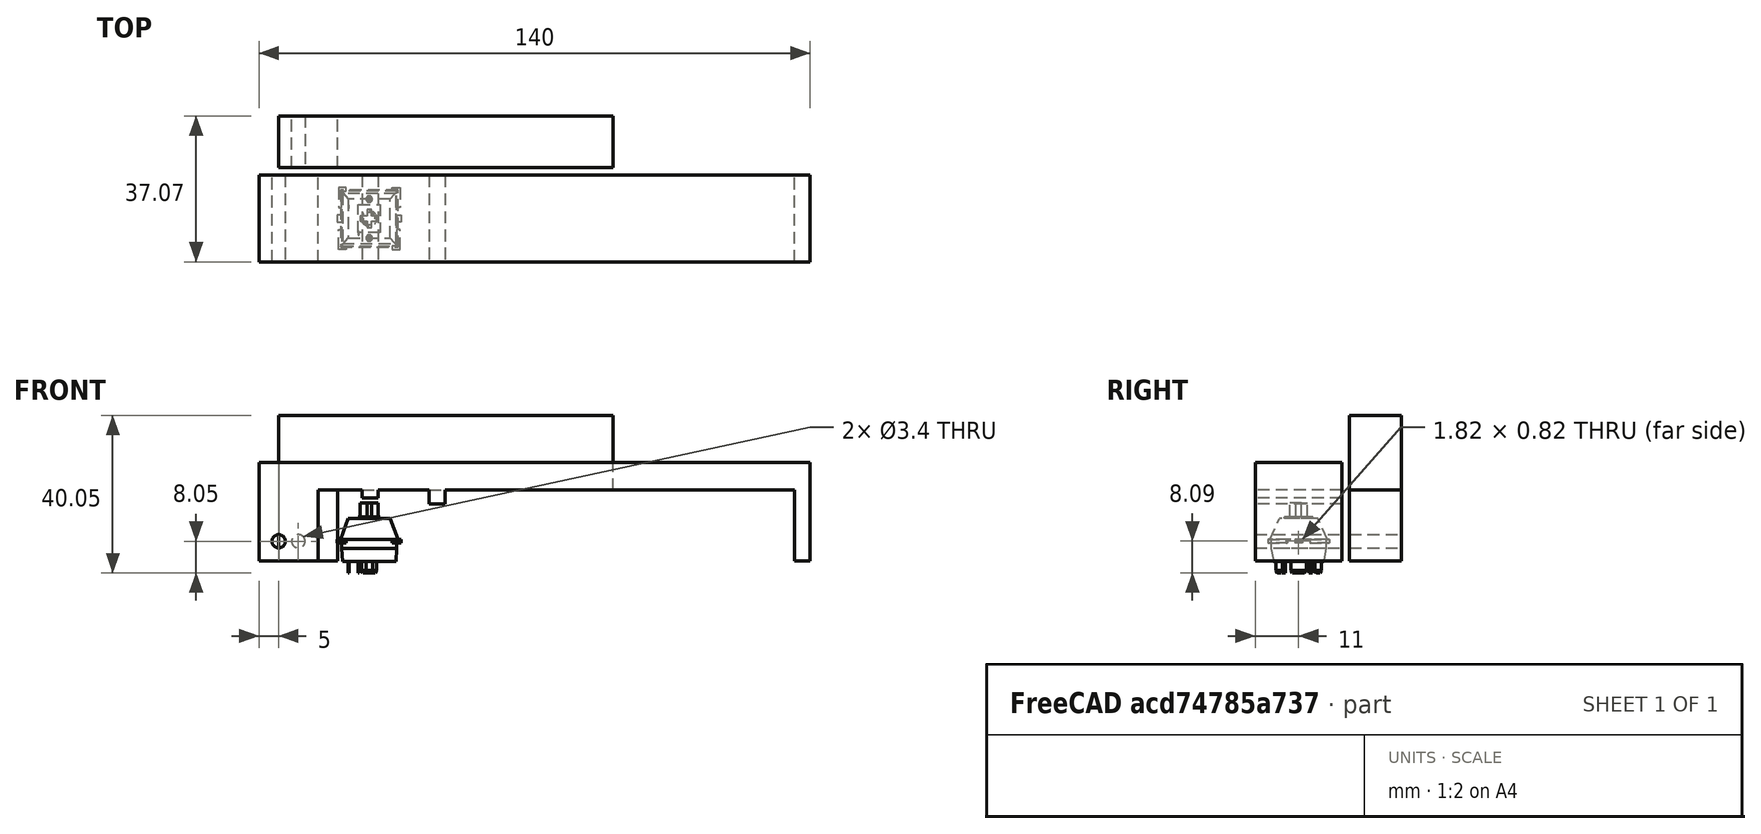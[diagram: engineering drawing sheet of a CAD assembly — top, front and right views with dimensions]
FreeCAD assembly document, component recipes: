
FREECAD ASSEMBLY — COMPONENT RECIPES ("ProtoKeyboardPiano")

This assembly document has 2 components, labeled P0..P1 below (a component is one placed body or linked part). 2 of them carry a construction recipe — the FreeCAD feature program that regenerates the part from scratch, quoted from this document or its linked companion documents; the rest are supplied as boundary geometry only. No exploded tour is included for this assembly.
COMPONENT P0 — recipe-attached ("Part001", modeled in this document).
Construction recipe (the document's own serialized feature program — sketch geometry with constraints, then the solid features built on it; lengths are millimeters unless a unit is written):

FEATURE [Sketcher::SketchObject] Sketch
  ArcFitTolerance = 1e-06
  AttachmentSupport = -> [XZ_Plane]
  FullyConstrained = true
  MakeInternals = false
  MapMode = 5
  Placement = pos=(0,0,0) rot=(1,0,0;1.5708rad)
  sketch-geometry (5):
    g0: Circle CenterX=0 CenterY=0 CenterZ=0 NormalX=0 NormalY=0 NormalZ=1 AngleXU=0 Radius=1.7
    g1: LineSegment StartX=-5 StartY=-5 StartZ=0 EndX=-5 EndY=20 EndZ=0
    g2: LineSegment StartX=-5 StartY=20 StartZ=0 EndX=135 EndY=20 EndZ=0
    g3: LineSegment StartX=135 StartY=20 StartZ=0 EndX=135 EndY=-5 EndZ=0
    g4: LineSegment StartX=135 StartY=-5 StartZ=0 EndX=-5 EndY=-5 EndZ=0
  constraints (14):
    c: Coincident(g0,g-1)
    c: Diameter(g0) = 3.4
    c: Vertical(g1)
    c: Coincident(g1,g2)
    c: Horizontal(g2)
    c: Coincident(g2,g3)
    c: Vertical(g3)
    c: Coincident(g3,g4)
    c: Coincident(g4,g1)
    c: Horizontal(g4)
    c: DistanceX(g2,g2) = 140
    c: DistanceX(g1,g0) = 5
    c: DistanceY(g1,g0) = 5
    c: DistanceY(g3,g3) = 25
FEATURE [PartDesign::Pad] Pad
  Direction = (0,-1,2e-16)
  Length = 22
  Length2 = 10
  Midplane = true
  Placement = pos=(0,0,0) rot=(1,0,0;1.5708rad)
  Profile = -> Sketch
  ReferenceAxis = -> Sketch [N_Axis]
  Refine = true
  Suppressed = false
  Type = 0
FEATURE [Sketcher::SketchObject] Sketch001
  ArcFitTolerance = 1e-06
  AttachmentSupport = -> [XZ_Plane]
  ExternalGeometry = -> [Pad]
  FullyConstrained = true
  MakeInternals = false
  MapMode = 5
  Placement = pos=(0,0,0) rot=(1,0,0;1.5708rad)
  sketch-geometry (4):
    g0: LineSegment StartX=10 StartY=-5 StartZ=0 EndX=131 EndY=-5 EndZ=0
    g1: LineSegment StartX=131 StartY=-5 StartZ=0 EndX=131 EndY=13 EndZ=0
    g2: LineSegment StartX=131 StartY=13 StartZ=0 EndX=10 EndY=13 EndZ=0
    g3: LineSegment StartX=10 StartY=13 StartZ=0 EndX=10 EndY=-5 EndZ=0
  constraints (12):
    c: Coincident(g0,g1)
    c: Coincident(g1,g2)
    c: Coincident(g2,g3)
    c: Coincident(g3,g0)
    c: Horizontal(g0)
    c: Horizontal(g2)
    c: Vertical(g1)
    c: Vertical(g3)
    c: PointOnObject(g0,g-3)
    c: Distance(g-3,g0) = 4
    c: DistanceY(g1,g1) = 18
    c: DistanceX(g-1,g0) = 10
FEATURE [PartDesign::Pocket] Pocket
  BaseFeature = -> Pad
  Direction = (0,1,-2e-16)
  Length = 5
  Length2 = 5
  Midplane = true
  Placement = pos=(0,0,0) rot=(1,0,0;1.5708rad)
  Profile = -> Sketch001
  ReferenceAxis = -> Sketch001 [N_Axis]
  Refine = true
  Suppressed = false
  Type = 1
FEATURE [Sketcher::SketchObject] Sketch002
  ArcFitTolerance = 1e-06
  AttachmentSupport = -> [XZ_Plane]
  ExternalGeometry = -> [Pocket]
  FullyConstrained = false
  MakeInternals = false
  MapMode = 5
  Placement = pos=(0,0,0) rot=(1,0,0;1.5708rad)
  sketch-geometry (23):
    g0: LineSegment [constr] StartX=0 StartY=0 StartZ=0 EndX=0 EndY=13 EndZ=0
    g1: LineSegment [constr] StartX=0 StartY=0 StartZ=0 EndX=1.14262 EndY=12.9497 EndZ=0
    g2: LineSegment [constr] StartX=1.14262 StartY=12.9497 StartZ=0 EndX=131 EndY=1.49168 EndZ=0
    g3: LineSegment [constr] StartX=23.2391 StartY=13 StartZ=0 EndX=23.2391 EndY=11 EndZ=0
    g4: LineSegment [constr] StartX=40.2391 StartY=13 StartZ=0 EndX=40.2391 EndY=9.5 EndZ=0
    g5: LineSegment StartX=21.2391 StartY=11 StartZ=0 EndX=25.2391 EndY=11 EndZ=0
    g6: LineSegment StartX=25.2391 StartY=11 StartZ=0 EndX=25.2391 EndY=13 EndZ=0
    g7: LineSegment StartX=25.2391 StartY=13 StartZ=0 EndX=21.2391 EndY=13 EndZ=0
    g8: LineSegment StartX=21.2391 StartY=13 StartZ=0 EndX=21.2391 EndY=11 EndZ=0
    g9: GeomPoint [constr] X=23.2391 Y=12 Z=0
    g10: LineSegment StartX=38.2391 StartY=9.5 StartZ=0 EndX=42.2391 EndY=9.5 EndZ=0
    g11: LineSegment StartX=42.2391 StartY=9.5 StartZ=0 EndX=42.2391 EndY=13 EndZ=0
    g12: LineSegment StartX=42.2391 StartY=13 StartZ=0 EndX=38.2391 EndY=13 EndZ=0
    g13: LineSegment StartX=38.2391 StartY=13 StartZ=0 EndX=38.2391 EndY=9.5 EndZ=0
    g14: GeomPoint [constr] X=40.2391 Y=11.25 Z=0
    g15: LineSegment [constr] StartX=0 StartY=13 StartZ=0 EndX=131 EndY=13 EndZ=0
    g16: LineSegment [constr] StartX=131 StartY=13 StartZ=0 EndX=131 EndY=1.49168 EndZ=0
    g17: LineSegment [constr] StartX=80 StartY=13 StartZ=0 EndX=80 EndY=-14.9258 EndZ=0
    g18: LineSegment [constr] StartX=0 StartY=0 StartZ=0 EndX=1.94118 EndY=16.5 EndZ=0
    g19: LineSegment [constr] StartX=1.94118 StartY=16.5 StartZ=0 EndX=80 EndY=7.31663 EndZ=0
    g20: LineSegment [constr] StartX=0 StartY=11.9944 StartZ=0 EndX=80 EndY=11.9944 EndZ=0
    g21: LineSegment [constr] StartX=57.2391 StartY=11.9944 StartZ=0 EndX=57.2391 EndY=9.99439 EndZ=0
    g22: LineSegment [constr] StartX=74.2391 StartY=11.9944 StartZ=0 EndX=74.2391 EndY=7.99439 EndZ=0
  constraints (68):
    c: Coincident(g0,g-1)
    c: PointOnObject(g0,g-2)
    c: Coincident(g0,g1)
    c: Coincident(g1,g2)
    c: Perpendicular(g2,g1,g1) = 1.5708
    c: Equal(g0,g1)
    c: PointOnObject(g3,g2)
    c: Vertical(g3)
    c: PointOnObject(g4,g2)
    c: Vertical(g4)
    c: Distance(g3,g3) = 2
    c: Distance(g4,g4) = 3.5
    c: DistanceX(g0,g3) = 23.2391
    c: DistanceX(g0,g4) = 40.2391
    c: Coincident(g5,g6)
    c: Coincident(g6,g7)
    c: Coincident(g7,g8)
    c: Coincident(g8,g5)
    c: Horizontal(g5)
    c: Horizontal(g7)
    c: Vertical(g6)
    c: Vertical(g8)
    c: Symmetric(g7,g5,g9)
    c: Symmetric(g3,g3,g9)
    c: Coincident(g10,g11)
    c: Coincident(g11,g12)
    c: Coincident(g12,g13)
    c: Coincident(g13,g10)
    c: Horizontal(g10)
    c: Horizontal(g12)
    c: Vertical(g11)
    c: Vertical(g13)
    c: Symmetric(g12,g10,g14)
    c: Symmetric(g4,g4,g14)
    c: Equal(g12,g7)
    c: Distance(g7,g7) = 4
    c: Coincident(g15,g0)
    c: Horizontal(g15)
    c: PointOnObject(g6,g15)
    c: PointOnObject(g3,g5)
    c: PointOnObject(g11,g15)
    c: PointOnObject(g4,g10)
    c: Coincident(g16,g15)
    c: Coincident(g16,g2)
    c: Perpendicular(g15,g16)
    c: Vertical(g17)
    c: DistanceX(g17,g-4) = 55
    c: Coincident(g15,g-3)
    c: PointOnObject(g17,g15)
    c: Coincident(g18,g0)
    c: Coincident(g19,g18)
    c: Perpendicular(g19,g18)
    c: PointOnObject(g19,g17)
    c: PointOnObject(g20,g-2)
    c: Horizontal(g20)
    c: PointOnObject(g20,g17)
    c: PointOnObject(g21,g20)
    c: PointOnObject(g21,g19)
    c: Vertical(g21)
    c: PointOnObject(g22,g20)
    c: PointOnObject(g22,g19)
    c: Vertical(g22)
    c: Distance(g21,g21) = 2
    c: Distance(g22,g22) = 4
    c: DistanceX(g3,g4) = 17
    c: DistanceX(g4,g21) = 17
    c: DistanceX(g21,g22) = 17
    c: DistanceY(g16,g16) = 11.5083
FEATURE [PartDesign::Pad] Pad001
  BaseFeature = -> Pocket
  Direction = (0,-1,2e-16)
  Length = 22
  Length2 = 10
  Midplane = true
  Placement = pos=(0,0,0) rot=(1,0,0;1.5708rad)
  Profile = -> Sketch002
  ReferenceAxis = -> Sketch002 [N_Axis]
  Refine = true
  Suppressed = false
  Type = 0
FEATURE [PartDesign::Body] Body  label="Corps"
  AllowCompound = false
  Group = -> [Sketch,Pad,Sketch001,Pocket,Sketch002,Pad001]
  Origin = -> Origin
  Tip = -> Pad001
COMPONENT P1 — recipe-attached ("Part002", modeled in this document).
Construction recipe (the document's own serialized feature program — sketch geometry with constraints, then the solid features built on it; lengths are millimeters unless a unit is written):

FEATURE [Sketcher::SketchObject] Sketch004
  ArcFitTolerance = 1e-06
  AttachmentSupport = -> [XZ_Plane003]
  FullyConstrained = true
  MakeInternals = false
  MapMode = 5
  Placement = pos=(0,0,0) rot=(1,0,0;1.5708rad)
  sketch-geometry (5):
    g0: Circle CenterX=0 CenterY=0 CenterZ=0 NormalX=0 NormalY=0 NormalZ=1 AngleXU=0 Radius=1.7
    g1: LineSegment StartX=-5 StartY=-5 StartZ=0 EndX=80 EndY=-5 EndZ=0
    g2: LineSegment StartX=80 StartY=-5 StartZ=0 EndX=80 EndY=32 EndZ=0
    g3: LineSegment StartX=80 StartY=32 StartZ=0 EndX=-5 EndY=32 EndZ=0
    g4: LineSegment StartX=-5 StartY=32 StartZ=0 EndX=-5 EndY=-5 EndZ=0
  constraints (14):
    c: Coincident(g0,g-1)
    c: Diameter(g0) = 3.4
    c: Coincident(g1,g2)
    c: Coincident(g2,g3)
    c: Coincident(g3,g4)
    c: Coincident(g4,g1)
    c: Horizontal(g1)
    c: Horizontal(g3)
    c: Vertical(g2)
    c: Vertical(g4)
    c: DistanceX(g1,g0) = 5
    c: DistanceY(g1,g0) = 5
    c: DistanceX(g3,g3) = 85
    c: DistanceY(g2,g2) = 37
FEATURE [PartDesign::Pad] Pad002
  Direction = (0,-1,2e-16)
  Length = 13.1429
  Length2 = 10
  Midplane = true
  Placement = pos=(0,0,0) rot=(1,0,0;1.5708rad)
  Profile = -> Sketch004
  ReferenceAxis = -> Sketch004 [N_Axis]
  Refine = true
  Suppressed = false
  Type = 0
  expr: Length = Sketch003.Constraints.LNoire
FEATURE [Sketcher::SketchObject] Sketch005
  ArcFitTolerance = 1e-06
  AttachmentSupport = -> [XZ_Plane003]
  ExternalGeometry = -> [Pad002]
  FullyConstrained = true
  MakeInternals = false
  MapMode = 5
  Placement = pos=(0,0,0) rot=(1,0,0;1.5708rad)
  sketch-geometry (4):
    g0: LineSegment StartX=10 StartY=-5 StartZ=0 EndX=80 EndY=-5 EndZ=0
    g1: LineSegment StartX=80 StartY=-5 StartZ=0 EndX=80 EndY=13 EndZ=0
    g2: LineSegment StartX=80 StartY=13 StartZ=0 EndX=10 EndY=13 EndZ=0
    g3: LineSegment StartX=10 StartY=13 StartZ=0 EndX=10 EndY=-5 EndZ=0
  constraints (11):
    c: Coincident(g0,g1)
    c: Coincident(g1,g2)
    c: Coincident(g2,g3)
    c: Coincident(g3,g0)
    c: Horizontal(g0)
    c: Horizontal(g2)
    c: Vertical(g1)
    c: Vertical(g3)
    c: Coincident(g-3,g0)
    c: DistanceX(g-1,g0) = 10
    c: DistanceY(g1,g1) = 18
FEATURE [PartDesign::Pocket] Pocket001
  BaseFeature = -> Pad002
  Direction = (0,1,-2e-16)
  Length = 5
  Length2 = 5
  Midplane = true
  Placement = pos=(0,0,0) rot=(1,0,0;1.5708rad)
  Profile = -> Sketch005
  ReferenceAxis = -> Sketch005 [N_Axis]
  Refine = true
  Suppressed = false
  Type = 1
FEATURE [Sketcher::SketchObject] Sketch006
  ArcFitTolerance = 1e-06
  AttachmentSupport = -> [XZ_Plane003]
  ExternalGeometry = -> [Pocket001]
  FullyConstrained = false
  MakeInternals = false
  MapMode = 5
  Placement = pos=(0,0,0) rot=(1,0,0;1.5708rad)
  sketch-geometry (7):
    g0: LineSegment [constr] StartX=0 StartY=0 StartZ=0 EndX=0.450484 EndY=9.78913 EndZ=0
    g1: LineSegment [constr] StartX=0.450484 StartY=9.78913 StartZ=0 EndX=79.8314 EndY=6.13611 EndZ=0
    g2: LineSegment [constr] StartX=0 StartY=0 StartZ=0 EndX=0 EndY=9.79949 EndZ=0
    g3: LineSegment [constr] StartX=0 StartY=9.79949 StartZ=0 EndX=80 EndY=9.79949 EndZ=0
    g4: LineSegment [constr] StartX=80 StartY=9.79949 StartZ=0 EndX=79.8314 EndY=6.13611 EndZ=0
    g5: LineSegment [constr] StartX=43.6859 StartY=9.79949 StartZ=0 EndX=43.6859 EndY=7.79949 EndZ=0
    g6: LineSegment [constr] StartX=76.2813 StartY=9.79949 StartZ=0 EndX=76.2813 EndY=6.29949 EndZ=0
  constraints (21):
    c: Coincident(g0,g-1)
    c: Coincident(g1,g0)
    c: Perpendicular(g0,g1)
    c: Coincident(g2,g0)
    c: PointOnObject(g2,g-2)
    c: Coincident(g3,g2)
    c: Horizontal(g3)
    c: Coincident(g4,g3)
    c: Coincident(g4,g1)
    c: Perpendicular(g4,g1)
    c: Distance(g4,g4) = 3.66725
    c: Equal(g2,g0)
    c: PointOnObject(g3,g-3)
    c: PointOnObject(g5,g3)
    c: PointOnObject(g5,g1)
    c: Vertical(g5)
    c: PointOnObject(g6,g3)
    c: PointOnObject(g6,g1)
    c: Vertical(g6)
    c: DistanceY(g6,g6) = 3.5
    c: DistanceY(g5,g5) = 2
FEATURE [PartDesign::Body] Body002  label="Corps002"
  AllowCompound = false
  Group = -> [Sketch004,Pad002,Sketch005,Pocket001,Sketch006]
  Origin = -> Origin003
  Placement = pos=(5,19.5,0) rot=(0,0,1;0rad)
  Tip = -> Pocket001
PROVENANCE & LICENSES
A FreeCAD (.FCStd) document from a public repository crawl; recipes are the document's own serialized feature recipes (and, for linked parts, companion documents' recipes).
License: as declared in the source repository (recorded in the dataset sidecar).
